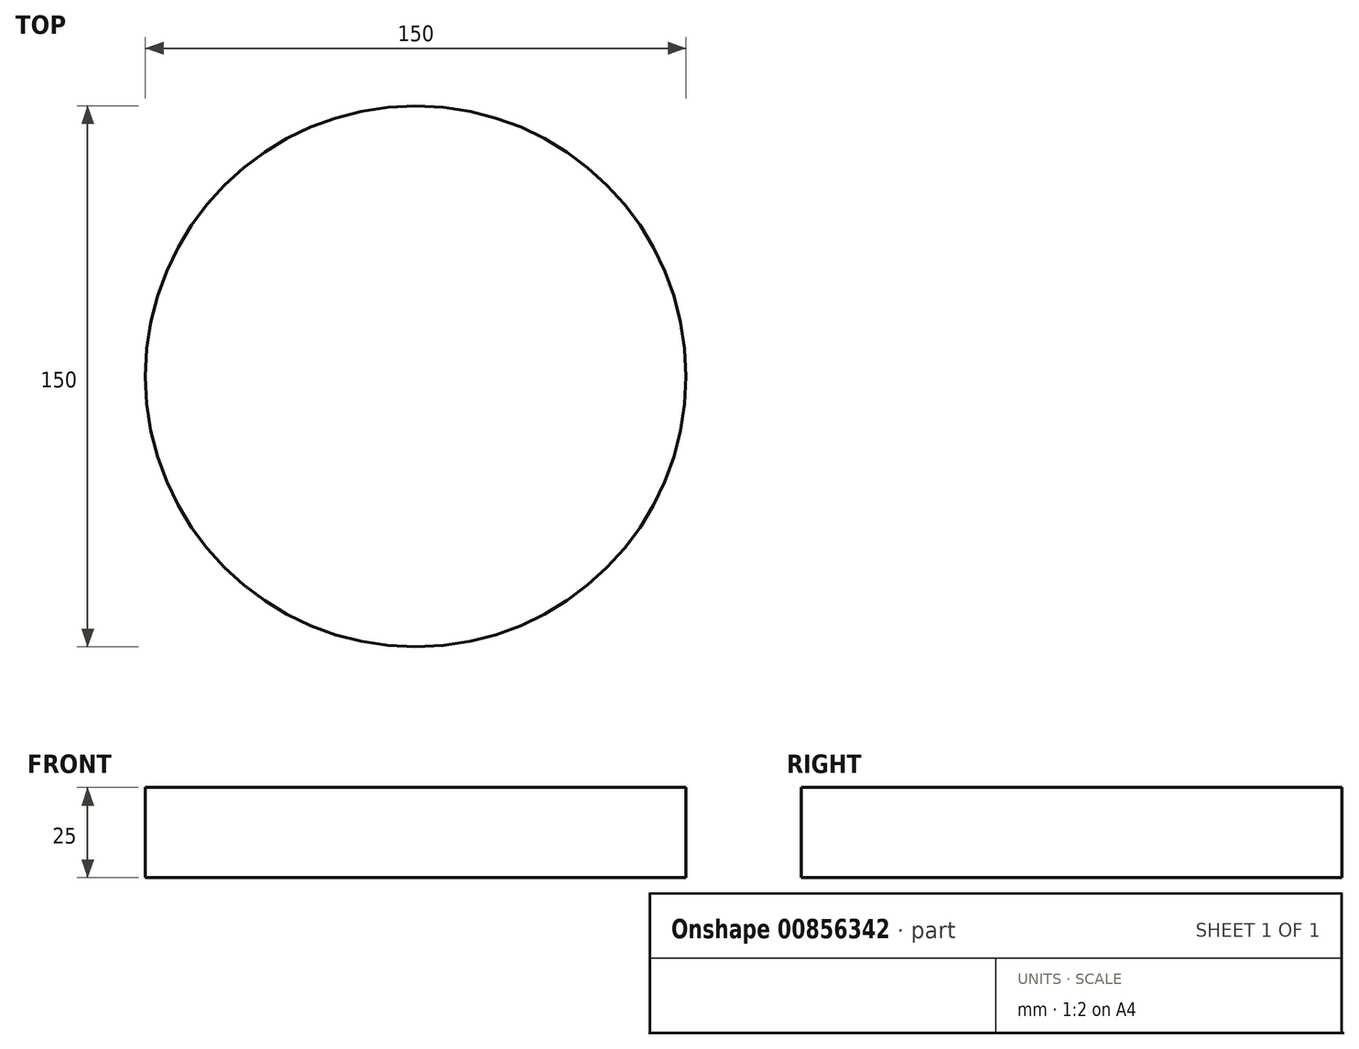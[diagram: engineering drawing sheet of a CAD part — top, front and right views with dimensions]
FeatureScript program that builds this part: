
annotation { "Feature Type Name" : "Feature", "Feature Type Description" : "" }
export const myFeature = defineFeature(function(context is Context, id is Id, definition is map)
    precondition{}
    {
        {
            var Q0;
            Q0=qCreatedBy(makeId("Top.planeOp"),FACE);
            var sketch = newSketch(context, id + "F0", { "sketchPlane" : qUnion([Q0])});
            skCircle(sketch, "E0", {"center": v(0, 0) * mm, "radius": 75 * mm});
            skSolve(sketch);
        }
        {
            var Q0;
            Q0=makeQuery(id+"F0.imprint","IMPRINT",FACE,{"disambiguationData":[TD([[makeQuery(id+"F0.imprint","IMPRINT",EDGE,{"derivedFrom":sQuery(id+"F0.wireOp",EDGE,"E0")}),1.0]])]});
            extrude(context, id + "F1", {"entities" : qUnion([Q0]), "depth" : 25 * mm, "offsetDistance" : 25 * mm});
        }
    });
